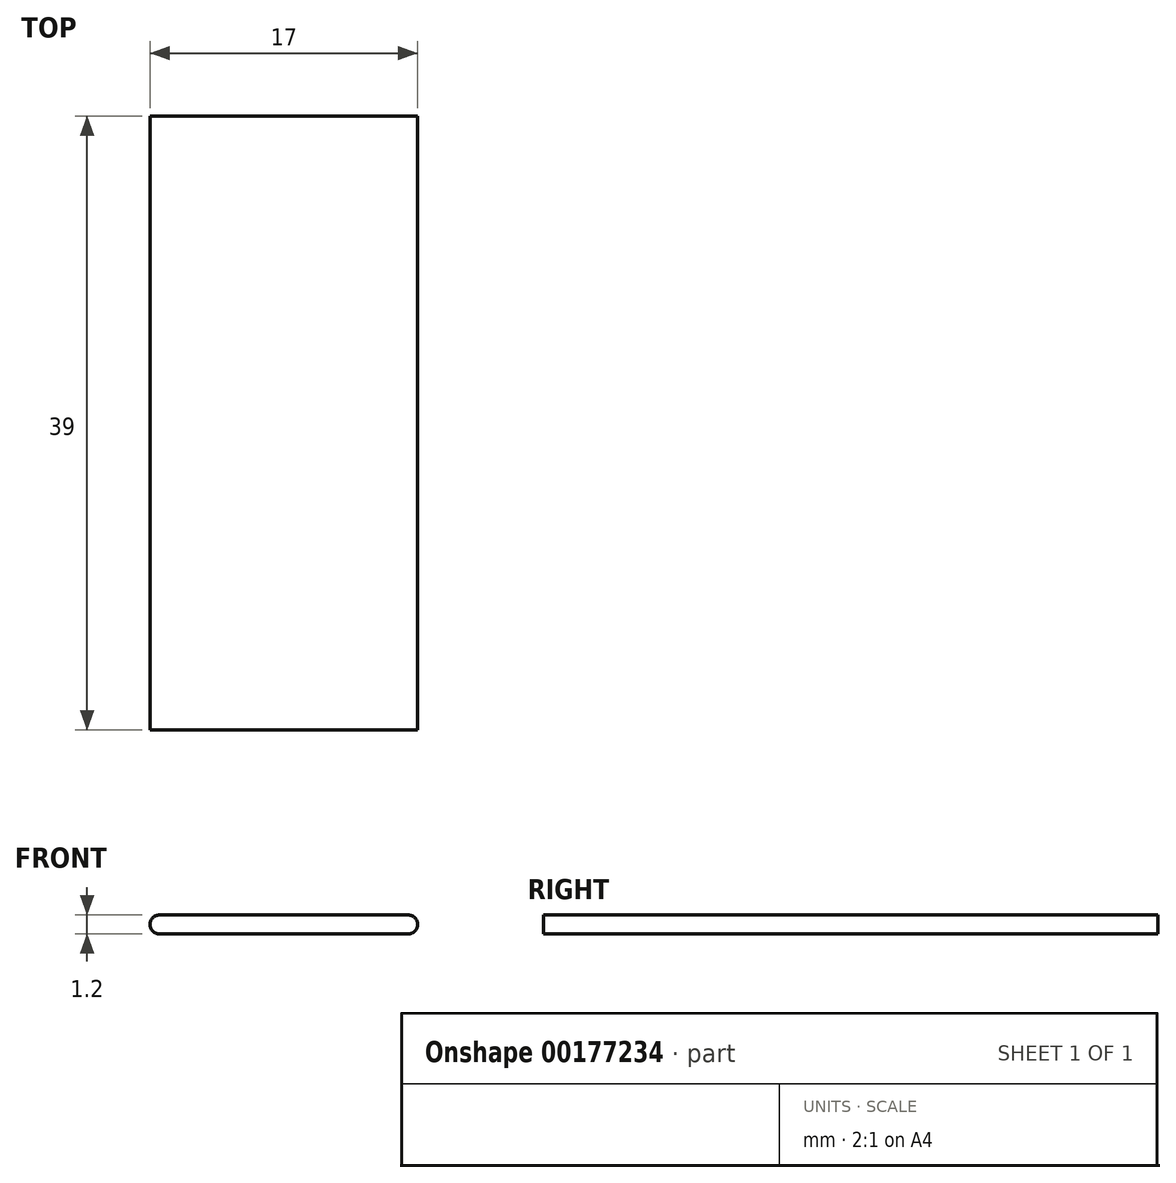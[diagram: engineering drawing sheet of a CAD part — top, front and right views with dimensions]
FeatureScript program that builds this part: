
annotation { "Feature Type Name" : "Feature", "Feature Type Description" : "" }
export const myFeature = defineFeature(function(context is Context, id is Id, definition is map)
    precondition{}
    {
        {
            var Q0;
            Q0=qCreatedBy(makeId("Front.planeOp"),FACE);
            var sketch = newSketch(context, id + "F0", { "sketchPlane" : qUnion([Q0])});
            skLineSegment(sketch, "E0.bottom", {"start": v(-8.5, 0.6) * mm, "end": v(8.5, 0.6) * mm});
            skLineSegment(sketch, "E0.top", {"start": v(-8.5, -0.6) * mm, "end": v(8.5, -0.6) * mm});
            skLineSegment(sketch, "E0.left", {"start": v(-8.5, 0.6) * mm, "end": v(-8.5, -0.6) * mm});
            skLineSegment(sketch, "E0.right", {"start": v(8.5, 0.6) * mm, "end": v(8.5, -0.6) * mm});
            skPoint(sketch, "E0.middle", {"position": v(0, 0) * mm});
            skSolve(sketch);
        }
        {
            var Q0;
            Q0=makeQuery(id+"F0.imprint","IMPRINT",FACE,{"disambiguationData":[TD([[makeQuery(id+"F0.imprint","IMPRINT",EDGE,{"derivedFrom":sQuery(id+"F0.wireOp",EDGE,"E0.bottom")}),-1.0]])]});
            extrude(context, id + "F1", {"entities" : qUnion([Q0]), "depth" : 39 * mm});
        }
        {
            var Q0;
            Q0=makeQuery(id+"F1.opExtrude","SWEPT_EDGE",EDGE,{"disambiguationData":[OSD([sQuery(id+"F0.wireOp",EDGE,"E0.bottom"),sQuery(id+"F0.wireOp",EDGE,"E0.right")])]});
            var Q1;
            Q1=makeQuery(id+"F1.opExtrude","SWEPT_EDGE",EDGE,{"disambiguationData":[OSD([sQuery(id+"F0.wireOp",EDGE,"E0.bottom"),sQuery(id+"F0.wireOp",EDGE,"E0.left")])]});
            var Q2;
            Q2=makeQuery(id+"F1.opExtrude","SWEPT_EDGE",EDGE,{"disambiguationData":[OSD([sQuery(id+"F0.wireOp",EDGE,"E0.top"),sQuery(id+"F0.wireOp",EDGE,"E0.right")])]});
            var Q3;
            Q3=makeQuery(id+"F1.opExtrude","SWEPT_EDGE",EDGE,{"disambiguationData":[OSD([sQuery(id+"F0.wireOp",EDGE,"E0.top"),sQuery(id+"F0.wireOp",EDGE,"E0.left")])]});
            fillet(context, id + "F2", {"entities" : qUnion([Q0, Q1, Q2, Q3]), "radius" : 0.6 * mm, "tangentPropagation" : true, "allowEdgeOverflow" : false});
        }
    });
